annotation { "Feature Type Name" : "Feature", "Feature Type Description" : "" }
export const myFeature = defineFeature(function(context is Context, id is Id, definition is map)
    precondition{}
    {
        {
            var Q0;
            Q0=qCreatedBy(makeId("Top.planeOp"),FACE);
            var sketch = newSketch(context, id + "F0", { "sketchPlane" : qUnion([Q0])});
            skLineSegment(sketch, "E0.bottom", {"start": v(76.5, 51) * mm, "end": v(57.38, 51) * mm});
            skLineSegment(sketch, "E0.top", {"start": v(76.5, -51) * mm, "end": v(-76.5, -51) * mm});
            skLineSegment(sketch, "E0.left", {"start": v(76.5, 51) * mm, "end": v(76.5, -51) * mm});
            skLineSegment(sketch, "E0.right", {"start": v(-76.5, 51) * mm, "end": v(-76.5, 38.25) * mm});
            skPoint(sketch, "E0.middle", {"position": v(0, 0) * mm});
            skLineSegment(sketch, "E1", {"start": v(0, 51) * mm, "end": v(-19.12, 51) * mm});
            skLineSegment(sketch, "E2", {"start": v(-38.25, 51) * mm, "end": v(-57.38, 51) * mm});
            skLineSegment(sketch, "E3", {"start": v(38.25, 51) * mm, "end": v(19.13, 51) * mm});
            skLineSegment(sketch, "E4", {"start": v(-57.38, 51) * mm, "end": v(-76.5, 51) * mm});
            skLineSegment(sketch, "E5", {"start": v(-19.12, 51) * mm, "end": v(-38.25, 51) * mm});
            skLineSegment(sketch, "E6", {"start": v(19.13, 51) * mm, "end": v(0, 51) * mm});
            skLineSegment(sketch, "E7", {"start": v(57.38, 51) * mm, "end": v(38.25, 51) * mm});
            skLineSegment(sketch, "E8", {"start": v(-76.5, 0) * mm, "end": v(-76.5, -12.75) * mm});
            skLineSegment(sketch, "E9", {"start": v(-76.5, 25.5) * mm, "end": v(-76.5, 12.75) * mm});
            skLineSegment(sketch, "E10", {"start": v(-76.5, 38.25) * mm, "end": v(-76.5, 25.5) * mm});
            skLineSegment(sketch, "E11", {"start": v(-76.5, 12.75) * mm, "end": v(-76.5, 0) * mm});
            skLineSegment(sketch, "E12", {"start": v(-76.5, -25.5) * mm, "end": v(-76.5, -38.25) * mm});
            skLineSegment(sketch, "E13", {"start": v(-76.5, -12.75) * mm, "end": v(-76.5, -25.5) * mm});
            skLineSegment(sketch, "E14", {"start": v(-76.5, -38.25) * mm, "end": v(-76.5, -51) * mm});
            skLineSegment(sketch, "E15", {"start": v(-57.38, 51) * mm, "end": v(-57.38, -51) * mm, "construction": true});
            skLineSegment(sketch, "E16", {"start": v(-57.38, -51) * mm, "end": v(-38.25, -51) * mm, "construction": true});
            skLineSegment(sketch, "E17", {"start": v(-38.25, -51) * mm, "end": v(-38.25, 51) * mm, "construction": true});
            skLineSegment(sketch, "E18", {"start": v(-19.12, 51) * mm, "end": v(-19.12, -51) * mm, "construction": true});
            skLineSegment(sketch, "E19", {"start": v(-19.12, -51) * mm, "end": v(0, -51) * mm, "construction": true});
            skLineSegment(sketch, "E20", {"start": v(0, -51) * mm, "end": v(0, 51) * mm, "construction": true});
            skLineSegment(sketch, "E21", {"start": v(19.13, 51) * mm, "end": v(19.13, -51) * mm, "construction": true});
            skLineSegment(sketch, "E22", {"start": v(19.13, -51) * mm, "end": v(38.25, -51) * mm, "construction": true});
            skLineSegment(sketch, "E23", {"start": v(38.25, -51) * mm, "end": v(38.25, 51) * mm, "construction": true});
            skLineSegment(sketch, "E24", {"start": v(57.38, 51) * mm, "end": v(57.38, -51) * mm, "construction": true});
            skLineSegment(sketch, "E25", {"start": v(57.37, -51) * mm, "end": v(-76.5, -51) * mm, "construction": true});
            skLineSegment(sketch, "E26", {"start": v(-76.5, -38.25) * mm, "end": v(76.5, -38.25) * mm, "construction": true});
            skLineSegment(sketch, "E27", {"start": v(76.5, -38.25) * mm, "end": v(76.5, -25.5) * mm, "construction": true});
            skLineSegment(sketch, "E28", {"start": v(76.5, -25.5) * mm, "end": v(-76.5, -25.5) * mm, "construction": true});
            skLineSegment(sketch, "E29", {"start": v(-76.5, -12.75) * mm, "end": v(76.5, -12.75) * mm, "construction": true});
            skLineSegment(sketch, "E30", {"start": v(76.5, -12.75) * mm, "end": v(76.5, 0) * mm, "construction": true});
            skLineSegment(sketch, "E31", {"start": v(76.5, 0) * mm, "end": v(-76.5, 0) * mm, "construction": true});
            skLineSegment(sketch, "E32", {"start": v(-76.5, 12.75) * mm, "end": v(76.5, 12.75) * mm, "construction": true});
            skLineSegment(sketch, "E33", {"start": v(76.5, 12.75) * mm, "end": v(76.5, 25.5) * mm, "construction": true});
            skLineSegment(sketch, "E34", {"start": v(76.5, 25.5) * mm, "end": v(-76.5, 25.5) * mm, "construction": true});
            skLineSegment(sketch, "E35", {"start": v(-76.5, 38.25) * mm, "end": v(76.5, 38.25) * mm, "construction": true});
            skCircle(sketch, "E36", {"center": v(-57.38, 38.25) * mm, "radius": 3.17 * mm});
            skCircle(sketch, "E37", {"center": v(-57.38, 25.5) * mm, "radius": 3.17 * mm});
            skCircle(sketch, "E38", {"center": v(-57.38, 12.75) * mm, "radius": 3.17 * mm});
            skCircle(sketch, "E39", {"center": v(-57.38, 0) * mm, "radius": 3.17 * mm});
            skCircle(sketch, "E40", {"center": v(-57.38, -12.75) * mm, "radius": 3.17 * mm});
            skCircle(sketch, "E41", {"center": v(-57.38, -25.5) * mm, "radius": 3.17 * mm});
            skCircle(sketch, "E42", {"center": v(-57.38, -38.25) * mm, "radius": 3.17 * mm});
            skCircle(sketch, "E43.1.0.0", {"center": v(-38.25, 38.25) * mm, "radius": 3.17 * mm});
            skCircle(sketch, "E43.1.0.1", {"center": v(-38.25, 25.5) * mm, "radius": 3.17 * mm});
            skCircle(sketch, "E43.1.0.2", {"center": v(-38.25, -38.25) * mm, "radius": 3.17 * mm});
            skCircle(sketch, "E43.1.0.3", {"center": v(-38.25, 12.75) * mm, "radius": 3.17 * mm});
            skCircle(sketch, "E43.1.0.4", {"center": v(-38.25, 0) * mm, "radius": 3.17 * mm});
            skCircle(sketch, "E43.1.0.5", {"center": v(-38.25, -12.75) * mm, "radius": 3.17 * mm});
            skCircle(sketch, "E43.1.0.6", {"center": v(-38.25, -25.5) * mm, "radius": 3.17 * mm});
            skCircle(sketch, "E43.2.0.0", {"center": v(-19.13, 38.25) * mm, "radius": 3.17 * mm});
            skCircle(sketch, "E43.2.0.1", {"center": v(-19.13, 25.5) * mm, "radius": 3.17 * mm});
            skCircle(sketch, "E43.2.0.2", {"center": v(-19.13, -38.25) * mm, "radius": 3.17 * mm});
            skCircle(sketch, "E43.2.0.3", {"center": v(-19.13, 12.75) * mm, "radius": 3.17 * mm});
            skCircle(sketch, "E43.2.0.4", {"center": v(-19.13, 0) * mm, "radius": 3.17 * mm});
            skCircle(sketch, "E43.2.0.5", {"center": v(-19.13, -12.75) * mm, "radius": 3.17 * mm});
            skCircle(sketch, "E43.2.0.6", {"center": v(-19.13, -25.5) * mm, "radius": 3.17 * mm});
            skCircle(sketch, "E43.3.0.0", {"center": v(0, 38.25) * mm, "radius": 3.17 * mm});
            skCircle(sketch, "E43.3.0.1", {"center": v(0, 25.5) * mm, "radius": 3.17 * mm});
            skCircle(sketch, "E43.3.0.2", {"center": v(0, -38.25) * mm, "radius": 3.17 * mm});
            skCircle(sketch, "E43.3.0.3", {"center": v(0, 12.75) * mm, "radius": 3.17 * mm});
            skCircle(sketch, "E43.3.0.4", {"center": v(0, 0) * mm, "radius": 3.17 * mm});
            skCircle(sketch, "E43.3.0.5", {"center": v(0, -12.75) * mm, "radius": 3.17 * mm});
            skCircle(sketch, "E43.3.0.6", {"center": v(0, -25.5) * mm, "radius": 3.17 * mm});
            skCircle(sketch, "E43.4.0.0", {"center": v(19.12, 38.25) * mm, "radius": 3.17 * mm});
            skCircle(sketch, "E43.4.0.1", {"center": v(19.12, 25.5) * mm, "radius": 3.17 * mm});
            skCircle(sketch, "E43.4.0.2", {"center": v(19.12, -38.25) * mm, "radius": 3.17 * mm});
            skCircle(sketch, "E43.4.0.3", {"center": v(19.12, 12.75) * mm, "radius": 3.17 * mm});
            skCircle(sketch, "E43.4.0.4", {"center": v(19.12, 0) * mm, "radius": 3.17 * mm});
            skCircle(sketch, "E43.4.0.5", {"center": v(19.12, -12.75) * mm, "radius": 3.17 * mm});
            skCircle(sketch, "E43.4.0.6", {"center": v(19.12, -25.5) * mm, "radius": 3.17 * mm});
            skCircle(sketch, "E43.5.0.0", {"center": v(38.25, 38.25) * mm, "radius": 3.17 * mm});
            skCircle(sketch, "E43.5.0.1", {"center": v(38.25, 25.5) * mm, "radius": 3.17 * mm});
            skCircle(sketch, "E43.5.0.2", {"center": v(38.25, -38.25) * mm, "radius": 3.17 * mm});
            skCircle(sketch, "E43.5.0.3", {"center": v(38.25, 12.75) * mm, "radius": 3.17 * mm});
            skCircle(sketch, "E43.5.0.4", {"center": v(38.25, 0) * mm, "radius": 3.17 * mm});
            skCircle(sketch, "E43.5.0.5", {"center": v(38.25, -12.75) * mm, "radius": 3.17 * mm});
            skCircle(sketch, "E43.5.0.6", {"center": v(38.25, -25.5) * mm, "radius": 3.17 * mm});
            skCircle(sketch, "E43.6.0.0", {"center": v(57.37, 38.25) * mm, "radius": 3.17 * mm});
            skCircle(sketch, "E43.6.0.1", {"center": v(57.37, 25.5) * mm, "radius": 3.17 * mm});
            skCircle(sketch, "E43.6.0.2", {"center": v(57.37, -38.25) * mm, "radius": 3.17 * mm});
            skCircle(sketch, "E43.6.0.3", {"center": v(57.37, 12.75) * mm, "radius": 3.17 * mm});
            skCircle(sketch, "E43.6.0.4", {"center": v(57.37, 0) * mm, "radius": 3.17 * mm});
            skCircle(sketch, "E43.6.0.5", {"center": v(57.37, -12.75) * mm, "radius": 3.17 * mm});
            skCircle(sketch, "E43.6.0.6", {"center": v(57.37, -25.5) * mm, "radius": 3.17 * mm});
            skLineSegment(sketch, "E43.direction1", {"start": v(-57.38, -38.25) * mm, "end": v(-38.25, -38.25) * mm, "construction": true});
            skSolve(sketch);
        }
        {
            var Q0;
            Q0=makeQuery(id+"F0.imprint","IMPRINT",FACE,{"disambiguationData":[TD([[makeQuery(id+"F0.imprint","IMPRINT",EDGE,{"derivedFrom":sQuery(id+"F0.wireOp",EDGE,"E0.bottom")}),1.0]])]});
            extrude(context, id + "F1", {"entities" : qUnion([Q0]), "depth" : 25 * mm, "offsetDistance" : 25 * mm});
        }
        {
            var Q0;
            Q0=makeQuery(id+"F1.opExtrude","CAP_FACE",FACE,{"disambiguationData":[OSD([sQuery(id+"F0.wireOp",EDGE,"E0.bottom"),sQuery(id+"F0.wireOp",EDGE,"E0.top"),sQuery(id+"F0.wireOp",EDGE,"E0.left"),sQuery(id+"F0.wireOp",EDGE,"E0.right"),sQuery(id+"F0.wireOp",EDGE,"E1"),sQuery(id+"F0.wireOp",EDGE,"E2"),sQuery(id+"F0.wireOp",EDGE,"E3"),sQuery(id+"F0.wireOp",EDGE,"E4"),sQuery(id+"F0.wireOp",EDGE,"E5"),sQuery(id+"F0.wireOp",EDGE,"E6"),sQuery(id+"F0.wireOp",EDGE,"E7"),sQuery(id+"F0.wireOp",EDGE,"E8"),sQuery(id+"F0.wireOp",EDGE,"E9"),sQuery(id+"F0.wireOp",EDGE,"E10"),sQuery(id+"F0.wireOp",EDGE,"E11"),sQuery(id+"F0.wireOp",EDGE,"E12"),sQuery(id+"F0.wireOp",EDGE,"E13"),sQuery(id+"F0.wireOp",EDGE,"E14"),sQuery(id+"F0.wireOp",EDGE,"E36"),sQuery(id+"F0.wireOp",EDGE,"E37"),sQuery(id+"F0.wireOp",EDGE,"E38"),sQuery(id+"F0.wireOp",EDGE,"E39"),sQuery(id+"F0.wireOp",EDGE,"E40"),sQuery(id+"F0.wireOp",EDGE,"E41"),sQuery(id+"F0.wireOp",EDGE,"E42"),sQuery(id+"F0.wireOp",EDGE,"E43.1.0.0"),sQuery(id+"F0.wireOp",EDGE,"E43.1.0.1"),sQuery(id+"F0.wireOp",EDGE,"E43.1.0.2"),sQuery(id+"F0.wireOp",EDGE,"E43.1.0.3"),sQuery(id+"F0.wireOp",EDGE,"E43.1.0.4"),sQuery(id+"F0.wireOp",EDGE,"E43.1.0.5"),sQuery(id+"F0.wireOp",EDGE,"E43.1.0.6"),sQuery(id+"F0.wireOp",EDGE,"E43.2.0.0"),sQuery(id+"F0.wireOp",EDGE,"E43.2.0.1"),sQuery(id+"F0.wireOp",EDGE,"E43.2.0.2"),sQuery(id+"F0.wireOp",EDGE,"E43.2.0.3"),sQuery(id+"F0.wireOp",EDGE,"E43.2.0.4"),sQuery(id+"F0.wireOp",EDGE,"E43.2.0.5"),sQuery(id+"F0.wireOp",EDGE,"E43.2.0.6"),sQuery(id+"F0.wireOp",EDGE,"E43.3.0.0"),sQuery(id+"F0.wireOp",EDGE,"E43.3.0.1"),sQuery(id+"F0.wireOp",EDGE,"E43.3.0.2"),sQuery(id+"F0.wireOp",EDGE,"E43.3.0.3"),sQuery(id+"F0.wireOp",EDGE,"E43.3.0.4"),sQuery(id+"F0.wireOp",EDGE,"E43.3.0.5"),sQuery(id+"F0.wireOp",EDGE,"E43.3.0.6"),sQuery(id+"F0.wireOp",EDGE,"E43.4.0.0"),sQuery(id+"F0.wireOp",EDGE,"E43.4.0.1"),sQuery(id+"F0.wireOp",EDGE,"E43.4.0.2"),sQuery(id+"F0.wireOp",EDGE,"E43.4.0.3"),sQuery(id+"F0.wireOp",EDGE,"E43.4.0.4"),sQuery(id+"F0.wireOp",EDGE,"E43.4.0.5"),sQuery(id+"F0.wireOp",EDGE,"E43.4.0.6"),sQuery(id+"F0.wireOp",EDGE,"E43.5.0.0"),sQuery(id+"F0.wireOp",EDGE,"E43.5.0.1"),sQuery(id+"F0.wireOp",EDGE,"E43.5.0.2"),sQuery(id+"F0.wireOp",EDGE,"E43.5.0.3"),sQuery(id+"F0.wireOp",EDGE,"E43.5.0.4"),sQuery(id+"F0.wireOp",EDGE,"E43.5.0.5"),sQuery(id+"F0.wireOp",EDGE,"E43.5.0.6"),sQuery(id+"F0.wireOp",EDGE,"E43.6.0.0"),sQuery(id+"F0.wireOp",EDGE,"E43.6.0.1"),sQuery(id+"F0.wireOp",EDGE,"E43.6.0.2"),sQuery(id+"F0.wireOp",EDGE,"E43.6.0.3"),sQuery(id+"F0.wireOp",EDGE,"E43.6.0.4"),sQuery(id+"F0.wireOp",EDGE,"E43.6.0.5"),sQuery(id+"F0.wireOp",EDGE,"E43.6.0.6")])],"isStart":false});
            var sketch = newSketch(context, id + "F2", { "sketchPlane" : qUnion([Q0])});
            skLineSegment(sketch, "E44.0", {"start": v(74.1, 48.6) * mm, "end": v(-74.1, 48.6) * mm});
            skLineSegment(sketch, "E44.1", {"start": v(74.1, 48.6) * mm, "end": v(74.1, -48.6) * mm});
            skLineSegment(sketch, "E44.2", {"start": v(74.1, -48.6) * mm, "end": v(-74.1, -48.6) * mm});
            skLineSegment(sketch, "E44.3", {"start": v(-74.1, 48.6) * mm, "end": v(-74.1, -48.6) * mm});
            skSolve(sketch);
        }
        {
            var Q0;
            Q0=makeQuery(id+"F2.imprint","IMPRINT",FACE,{"disambiguationData":[TD([[makeQuery(id+"F2.imprint","IMPRINT",EDGE,{"derivedFrom":sQuery(id+"F2.wireOp",EDGE,"E44.0")}),-1.0]])]});
            extrude(context, id + "F3", {"entities" : qUnion([Q0]), "operationType" : NewBodyOperationType.ADD, "depth" : 32.5 * mm, "offsetDistance" : 25 * mm});
        }
        {
            var Q0;
            Q0=makeQuery(id+"F1.opExtrude","CAP_FACE",FACE,{"disambiguationData":[OSD([sQuery(id+"F0.wireOp",EDGE,"E0.bottom"),sQuery(id+"F0.wireOp",EDGE,"E0.top"),sQuery(id+"F0.wireOp",EDGE,"E0.left"),sQuery(id+"F0.wireOp",EDGE,"E0.right"),sQuery(id+"F0.wireOp",EDGE,"E1"),sQuery(id+"F0.wireOp",EDGE,"E2"),sQuery(id+"F0.wireOp",EDGE,"E3"),sQuery(id+"F0.wireOp",EDGE,"E4"),sQuery(id+"F0.wireOp",EDGE,"E5"),sQuery(id+"F0.wireOp",EDGE,"E6"),sQuery(id+"F0.wireOp",EDGE,"E7"),sQuery(id+"F0.wireOp",EDGE,"E8"),sQuery(id+"F0.wireOp",EDGE,"E9"),sQuery(id+"F0.wireOp",EDGE,"E10"),sQuery(id+"F0.wireOp",EDGE,"E11"),sQuery(id+"F0.wireOp",EDGE,"E12"),sQuery(id+"F0.wireOp",EDGE,"E13"),sQuery(id+"F0.wireOp",EDGE,"E14"),sQuery(id+"F0.wireOp",EDGE,"E36"),sQuery(id+"F0.wireOp",EDGE,"E37"),sQuery(id+"F0.wireOp",EDGE,"E38"),sQuery(id+"F0.wireOp",EDGE,"E39"),sQuery(id+"F0.wireOp",EDGE,"E40"),sQuery(id+"F0.wireOp",EDGE,"E41"),sQuery(id+"F0.wireOp",EDGE,"E42"),sQuery(id+"F0.wireOp",EDGE,"E43.1.0.0"),sQuery(id+"F0.wireOp",EDGE,"E43.1.0.1"),sQuery(id+"F0.wireOp",EDGE,"E43.1.0.2"),sQuery(id+"F0.wireOp",EDGE,"E43.1.0.3"),sQuery(id+"F0.wireOp",EDGE,"E43.1.0.4"),sQuery(id+"F0.wireOp",EDGE,"E43.1.0.5"),sQuery(id+"F0.wireOp",EDGE,"E43.1.0.6"),sQuery(id+"F0.wireOp",EDGE,"E43.2.0.0"),sQuery(id+"F0.wireOp",EDGE,"E43.2.0.1"),sQuery(id+"F0.wireOp",EDGE,"E43.2.0.2"),sQuery(id+"F0.wireOp",EDGE,"E43.2.0.3"),sQuery(id+"F0.wireOp",EDGE,"E43.2.0.4"),sQuery(id+"F0.wireOp",EDGE,"E43.2.0.5"),sQuery(id+"F0.wireOp",EDGE,"E43.2.0.6"),sQuery(id+"F0.wireOp",EDGE,"E43.3.0.0"),sQuery(id+"F0.wireOp",EDGE,"E43.3.0.1"),sQuery(id+"F0.wireOp",EDGE,"E43.3.0.2"),sQuery(id+"F0.wireOp",EDGE,"E43.3.0.3"),sQuery(id+"F0.wireOp",EDGE,"E43.3.0.4"),sQuery(id+"F0.wireOp",EDGE,"E43.3.0.5"),sQuery(id+"F0.wireOp",EDGE,"E43.3.0.6"),sQuery(id+"F0.wireOp",EDGE,"E43.4.0.0"),sQuery(id+"F0.wireOp",EDGE,"E43.4.0.1"),sQuery(id+"F0.wireOp",EDGE,"E43.4.0.2"),sQuery(id+"F0.wireOp",EDGE,"E43.4.0.3"),sQuery(id+"F0.wireOp",EDGE,"E43.4.0.4"),sQuery(id+"F0.wireOp",EDGE,"E43.4.0.5"),sQuery(id+"F0.wireOp",EDGE,"E43.4.0.6"),sQuery(id+"F0.wireOp",EDGE,"E43.5.0.0"),sQuery(id+"F0.wireOp",EDGE,"E43.5.0.1"),sQuery(id+"F0.wireOp",EDGE,"E43.5.0.2"),sQuery(id+"F0.wireOp",EDGE,"E43.5.0.3"),sQuery(id+"F0.wireOp",EDGE,"E43.5.0.4"),sQuery(id+"F0.wireOp",EDGE,"E43.5.0.5"),sQuery(id+"F0.wireOp",EDGE,"E43.5.0.6"),sQuery(id+"F0.wireOp",EDGE,"E43.6.0.0"),sQuery(id+"F0.wireOp",EDGE,"E43.6.0.1"),sQuery(id+"F0.wireOp",EDGE,"E43.6.0.2"),sQuery(id+"F0.wireOp",EDGE,"E43.6.0.3"),sQuery(id+"F0.wireOp",EDGE,"E43.6.0.4"),sQuery(id+"F0.wireOp",EDGE,"E43.6.0.5"),sQuery(id+"F0.wireOp",EDGE,"E43.6.0.6")])],"isStart":true});
            var sketch = newSketch(context, id + "F4", { "sketchPlane" : qUnion([Q0])});
            skLineSegment(sketch, "E45.bottom", {"start": v(-76.5, 51) * mm, "end": v(76.5, 51) * mm});
            skLineSegment(sketch, "E45.top", {"start": v(-76.5, -51) * mm, "end": v(76.5, -51) * mm});
            skLineSegment(sketch, "E45.left", {"start": v(-76.5, 51) * mm, "end": v(-76.5, -51) * mm});
            skLineSegment(sketch, "E45.right", {"start": v(76.5, 51) * mm, "end": v(76.5, -51) * mm});
            skSolve(sketch);
        }
        {
            var Q0;
            Q0 = qSketchRegion(id + "F4", true);
            extrude(context, id + "F5", {"entities" : qUnion([Q0]), "operationType" : NewBodyOperationType.ADD, "depth" : 2.4 * mm, "offsetDistance" : 25 * mm});
        }
        {
            var Q0;
            Q0=makeQuery(id+"F5.opExtrude","CAP_FACE",FACE,{"disambiguationData":[OSD([sQuery(id+"F4.wireOp",EDGE,"E45.bottom"),sQuery(id+"F4.wireOp",EDGE,"E45.top"),sQuery(id+"F4.wireOp",EDGE,"E45.left"),sQuery(id+"F4.wireOp",EDGE,"E45.right")])],"isStart":false});
            var Q1;
            {var subQ0=sQuery(id+"F0.wireOp",EDGE,"E14");var subQ1=sQuery(id+"F0.wireOp",EDGE,"E0.top");Q1=makeQuery(id+"F5.boolean.opBoolean","MERGE",EDGE,{"derivedFrom":[makeQuery(id+"F3.boolean.opBoolean","MERGE",EDGE,{"derivedFrom":[makeQuery(id+"F1.opExtrude","SWEPT_EDGE",EDGE,{"disambiguationData":[OSD([subQ1,subQ0])]}),makeQuery(id+"F3.opExtrude","SWEPT_EDGE",EDGE,{"disambiguationData":[OSD([subQ1,sQuery(id+"F0.wireOp",EDGE,"E0.right"),sQuery(id+"F0.wireOp",EDGE,"E8"),sQuery(id+"F0.wireOp",EDGE,"E9"),sQuery(id+"F0.wireOp",EDGE,"E10"),sQuery(id+"F0.wireOp",EDGE,"E11"),sQuery(id+"F0.wireOp",EDGE,"E12"),sQuery(id+"F0.wireOp",EDGE,"E13"),subQ0])]})]}),makeQuery(id+"F5.opExtrude","SWEPT_EDGE",EDGE,{"disambiguationData":[OSD([sQuery(id+"F4.wireOp",EDGE,"E45.bottom"),sQuery(id+"F4.wireOp",EDGE,"E45.left")])]})]});}
            var Q2;
            {var subQ0=sQuery(id+"F0.wireOp",EDGE,"E4");var subQ1=sQuery(id+"F0.wireOp",EDGE,"E0.right");Q2=makeQuery(id+"F5.boolean.opBoolean","MERGE",EDGE,{"derivedFrom":[makeQuery(id+"F3.boolean.opBoolean","MERGE",EDGE,{"derivedFrom":[makeQuery(id+"F1.opExtrude","SWEPT_EDGE",EDGE,{"disambiguationData":[OSD([subQ1,subQ0])]}),makeQuery(id+"F3.opExtrude","SWEPT_EDGE",EDGE,{"disambiguationData":[OSD([sQuery(id+"F0.wireOp",EDGE,"E0.bottom"),subQ1,sQuery(id+"F0.wireOp",EDGE,"E1"),sQuery(id+"F0.wireOp",EDGE,"E2"),sQuery(id+"F0.wireOp",EDGE,"E3"),subQ0,sQuery(id+"F0.wireOp",EDGE,"E5"),sQuery(id+"F0.wireOp",EDGE,"E6"),sQuery(id+"F0.wireOp",EDGE,"E7"),sQuery(id+"F0.wireOp",EDGE,"E8"),sQuery(id+"F0.wireOp",EDGE,"E9"),sQuery(id+"F0.wireOp",EDGE,"E10"),sQuery(id+"F0.wireOp",EDGE,"E11"),sQuery(id+"F0.wireOp",EDGE,"E12"),sQuery(id+"F0.wireOp",EDGE,"E13"),sQuery(id+"F0.wireOp",EDGE,"E14")])]})]}),makeQuery(id+"F5.opExtrude","SWEPT_EDGE",EDGE,{"disambiguationData":[OSD([sQuery(id+"F4.wireOp",EDGE,"E45.top"),sQuery(id+"F4.wireOp",EDGE,"E45.left")])]})]});}
            var Q3;
            {var subQ0=sQuery(id+"F0.wireOp",EDGE,"E0.left");var subQ1=sQuery(id+"F0.wireOp",EDGE,"E0.bottom");Q3=makeQuery(id+"F5.boolean.opBoolean","MERGE",EDGE,{"derivedFrom":[makeQuery(id+"F3.boolean.opBoolean","MERGE",EDGE,{"derivedFrom":[makeQuery(id+"F1.opExtrude","SWEPT_EDGE",EDGE,{"disambiguationData":[OSD([subQ1,subQ0])]}),makeQuery(id+"F3.opExtrude","SWEPT_EDGE",EDGE,{"disambiguationData":[OSD([subQ1,subQ0,sQuery(id+"F0.wireOp",EDGE,"E1"),sQuery(id+"F0.wireOp",EDGE,"E2"),sQuery(id+"F0.wireOp",EDGE,"E3"),sQuery(id+"F0.wireOp",EDGE,"E4"),sQuery(id+"F0.wireOp",EDGE,"E5"),sQuery(id+"F0.wireOp",EDGE,"E6"),sQuery(id+"F0.wireOp",EDGE,"E7")])]})]}),makeQuery(id+"F5.opExtrude","SWEPT_EDGE",EDGE,{"disambiguationData":[OSD([sQuery(id+"F4.wireOp",EDGE,"E45.top"),sQuery(id+"F4.wireOp",EDGE,"E45.right")])]})]});}
            var Q4;
            {var subQ0=sQuery(id+"F0.wireOp",EDGE,"E0.left");var subQ1=sQuery(id+"F0.wireOp",EDGE,"E0.top");Q4=makeQuery(id+"F5.boolean.opBoolean","MERGE",EDGE,{"derivedFrom":[makeQuery(id+"F3.boolean.opBoolean","MERGE",EDGE,{"derivedFrom":[makeQuery(id+"F1.opExtrude","SWEPT_EDGE",EDGE,{"disambiguationData":[OSD([subQ1,subQ0])]}),makeQuery(id+"F3.opExtrude","SWEPT_EDGE",EDGE,{"disambiguationData":[OSD([subQ1,subQ0])]})]}),makeQuery(id+"F5.opExtrude","SWEPT_EDGE",EDGE,{"disambiguationData":[OSD([sQuery(id+"F4.wireOp",EDGE,"E45.bottom"),sQuery(id+"F4.wireOp",EDGE,"E45.right")])]})]});}
            fillet(context, id + "F6", {"entities" : qUnion([Q0, Q1, Q2, Q3, Q4]), "radius" : 2.5 * mm, "tangentPropagation" : true, "allowEdgeOverflow" : false});
        }
        {
            var Q0;
            Q0=makeQuery(id+"F3.opExtrude","CAP_FACE",FACE,{"disambiguationData":[OSD([sQuery(id+"F0.wireOp",EDGE,"E0.bottom"),sQuery(id+"F0.wireOp",EDGE,"E0.top"),sQuery(id+"F0.wireOp",EDGE,"E0.left"),sQuery(id+"F0.wireOp",EDGE,"E0.right"),sQuery(id+"F0.wireOp",EDGE,"E1"),sQuery(id+"F0.wireOp",EDGE,"E2"),sQuery(id+"F0.wireOp",EDGE,"E3"),sQuery(id+"F0.wireOp",EDGE,"E4"),sQuery(id+"F0.wireOp",EDGE,"E5"),sQuery(id+"F0.wireOp",EDGE,"E6"),sQuery(id+"F0.wireOp",EDGE,"E7"),sQuery(id+"F0.wireOp",EDGE,"E8"),sQuery(id+"F0.wireOp",EDGE,"E9"),sQuery(id+"F0.wireOp",EDGE,"E10"),sQuery(id+"F0.wireOp",EDGE,"E11"),sQuery(id+"F0.wireOp",EDGE,"E12"),sQuery(id+"F0.wireOp",EDGE,"E13"),sQuery(id+"F0.wireOp",EDGE,"E14"),sQuery(id+"F2.wireOp",EDGE,"E44.0"),sQuery(id+"F2.wireOp",EDGE,"E44.1"),sQuery(id+"F2.wireOp",EDGE,"E44.2"),sQuery(id+"F2.wireOp",EDGE,"E44.3")])],"isStart":false});
            var sketch = newSketch(context, id + "F7", { "sketchPlane" : qUnion([Q0])});
            skLineSegment(sketch, "E46.bottom", {"start": v(-76.5, 51) * mm, "end": v(76.5, 51) * mm});
            skLineSegment(sketch, "E46.top", {"start": v(-76.5, -51) * mm, "end": v(76.5, -51) * mm});
            skLineSegment(sketch, "E46.left", {"start": v(-76.5, 51) * mm, "end": v(-76.5, -51) * mm});
            skLineSegment(sketch, "E46.right", {"start": v(76.5, 51) * mm, "end": v(76.5, -51) * mm});
            skSolve(sketch);
        }
        {
            var Q0;
            Q0 = qSketchRegion(id + "F7", true);
            var Q1;
            Q1=makeQuery(id+"F5.opExtrude","CAP_FACE",FACE,{"disambiguationData":[OSD([sQuery(id+"F4.wireOp",EDGE,"E45.bottom"),sQuery(id+"F4.wireOp",EDGE,"E45.top"),sQuery(id+"F4.wireOp",EDGE,"E45.left"),sQuery(id+"F4.wireOp",EDGE,"E45.right")])],"isStart":false});
            extrude(context, id + "F8", {"entities" : qUnion([Q0]), "endBound" : BoundingType.UP_TO_SURFACE, "oppositeDirection" : true, "depth" : 25 * mm, "endBoundEntityFace" : qUnion([Q1]), "offsetDistance" : 25 * mm});
        }
        {
            var Q0;
            Q0=makeQuery(id+"F8.opExtrude","CAP_FACE",FACE,{"disambiguationData":[OSD([sQuery(id+"F7.wireOp",EDGE,"E46.bottom"),sQuery(id+"F7.wireOp",EDGE,"E46.top"),sQuery(id+"F7.wireOp",EDGE,"E46.left"),sQuery(id+"F7.wireOp",EDGE,"E46.right")])],"isStart":false});
            shell(context, id + "F9", {"entities" : qUnion([Q0]), "thickness" : 2.9 * mm, "oppositeDirection" : true});
        }
        {
            var Q0;
            Q0=makeQuery(id+"F8.opExtrude","CAP_FACE",FACE,{"disambiguationData":[OSD([sQuery(id+"F7.wireOp",EDGE,"E46.bottom"),sQuery(id+"F7.wireOp",EDGE,"E46.top"),sQuery(id+"F7.wireOp",EDGE,"E46.left"),sQuery(id+"F7.wireOp",EDGE,"E46.right")])],"isStart":true});
            fillet(context, id + "F10", {"entities" : qUnion([Q0]), "radius" : 5 * mm, "tangentPropagation" : true, "allowEdgeOverflow" : false});
        }
        {
            var Q0;
            Q0=makeQuery(id+"F8.opExtrude","CAP_FACE",FACE,{"disambiguationData":[OSD([sQuery(id+"F7.wireOp",EDGE,"E46.bottom"),sQuery(id+"F7.wireOp",EDGE,"E46.top"),sQuery(id+"F7.wireOp",EDGE,"E46.left"),sQuery(id+"F7.wireOp",EDGE,"E46.right")])],"isStart":true});
            var sketch = newSketch(context, id + "F11", { "sketchPlane" : qUnion([Q0])});
            skText(sketch, "E47", { "text": "ROUTER BITS", "fontName": "OpenSans-Bold.ttf"});
            const initialGuessF11  = {"E47": [-0.0709, -0.00018, 1, 0, 0.01591]};
            skSetInitialGuess(sketch, initialGuessF11);
            skSolve(sketch);
        }
        {
            var Q0;
            Q0=makeQuery(id+"F11.imprint","IMPRINT",FACE,{"disambiguationData":[TD([[makeQuery(id+"F11.imprint","IMPRINT",EDGE,{"derivedFrom":sQuery(id+"F11.wireOp",EDGE,"E47.sketch_text.stroke-0")}),-1.0]])]});
            var Q1;
            Q1=makeQuery(id+"F11.imprint","IMPRINT",FACE,{"disambiguationData":[TD([[makeQuery(id+"F11.imprint","IMPRINT",EDGE,{"derivedFrom":sQuery(id+"F11.wireOp",EDGE,"E47.sketch_text.stroke-19")}),-1.0]])]});
            var Q2;
            Q2=makeQuery(id+"F11.imprint","IMPRINT",FACE,{"disambiguationData":[TD([[makeQuery(id+"F11.imprint","IMPRINT",EDGE,{"derivedFrom":sQuery(id+"F11.wireOp",EDGE,"E47.sketch_text.stroke-33")}),-1.0]])]});
            var Q3;
            Q3=makeQuery(id+"F11.imprint","IMPRINT",FACE,{"disambiguationData":[TD([[makeQuery(id+"F11.imprint","IMPRINT",EDGE,{"derivedFrom":sQuery(id+"F11.wireOp",EDGE,"E47.sketch_text.stroke-48")}),-1.0]])]});
            var Q4;
            Q4=makeQuery(id+"F11.imprint","IMPRINT",FACE,{"disambiguationData":[TD([[makeQuery(id+"F11.imprint","IMPRINT",EDGE,{"derivedFrom":sQuery(id+"F11.wireOp",EDGE,"E47.sketch_text.stroke-56")}),-1.0]])]});
            var Q5;
            Q5=makeQuery(id+"F11.imprint","IMPRINT",FACE,{"disambiguationData":[TD([[makeQuery(id+"F11.imprint","IMPRINT",EDGE,{"derivedFrom":sQuery(id+"F11.wireOp",EDGE,"E47.sketch_text.stroke-68")}),-1.0]])]});
            var Q6;
            Q6=makeQuery(id+"F11.imprint","IMPRINT",FACE,{"disambiguationData":[TD([[makeQuery(id+"F11.imprint","IMPRINT",EDGE,{"derivedFrom":sQuery(id+"F11.wireOp",EDGE,"E47.sketch_text.stroke-87")}),-1.0]])]});
            var Q7;
            Q7=makeQuery(id+"F11.imprint","IMPRINT",FACE,{"disambiguationData":[TD([[makeQuery(id+"F11.imprint","IMPRINT",EDGE,{"derivedFrom":sQuery(id+"F11.wireOp",EDGE,"E47.sketch_text.stroke-112")}),-1.0]])]});
            var Q8;
            Q8=makeQuery(id+"F11.imprint","IMPRINT",FACE,{"disambiguationData":[TD([[makeQuery(id+"F11.imprint","IMPRINT",EDGE,{"derivedFrom":sQuery(id+"F11.wireOp",EDGE,"E47.sketch_text.stroke-116")}),-1.0]])]});
            var Q9;
            Q9=makeQuery(id+"F11.imprint","IMPRINT",FACE,{"disambiguationData":[TD([[makeQuery(id+"F11.imprint","IMPRINT",EDGE,{"derivedFrom":sQuery(id+"F11.wireOp",EDGE,"E47.sketch_text.stroke-124")}),-1.0]])]});
            extrude(context, id + "F12", {"entities" : qUnion([Q0, Q1, Q2, Q3, Q4, Q5, Q6, Q7, Q8, Q9]), "operationType" : NewBodyOperationType.REMOVE, "oppositeDirection" : true, "depth" : 1 * mm, "offsetDistance" : 25 * mm});
        }
        {
            var Q0;
            Q0=makeQuery(id+"F12.boolean.opBoolean","COPY",EDGE,{"derivedFrom":makeQuery(id+"F12.opExtrude","CAP_EDGE",EDGE,{"disambiguationData":[OSD([sQuery(id+"F11.wireOp",EDGE,"E47.sketch_text.stroke-9")])],"isStart":true})});
            var Q1;
            {var subQ0=sQuery(id+"F7.wireOp",EDGE,"E46.right");var subQ1=sQuery(id+"F7.wireOp",EDGE,"E46.left");var subQ2=sQuery(id+"F7.wireOp",EDGE,"E46.top");var subQ3=sQuery(id+"F7.wireOp",EDGE,"E46.bottom");Q1=makeQuery(id+"F12.boolean.opBoolean","SPLIT",FACE,{"disambiguationData":[TD([makeQuery(id+"F10.opFillet","BLEND_FACE",FACE,{"disambiguationData":[OSD([subQ3])]})])],"derivedFrom":makeQuery(id+"F8.opExtrude","CAP_FACE",FACE,{"disambiguationData":[OSD([subQ3,subQ2,subQ1,subQ0])],"isStart":true})});}
            var Q2;
            Q2=makeQuery(id+"F12.boolean.opBoolean","SPLIT",FACE,{"disambiguationData":[TD([makeQuery(id+"F12.opExtrude","SWEPT_FACE",FACE,{"disambiguationData":[OSD([sQuery(id+"F11.wireOp",EDGE,"E47.sketch_text.stroke-27")])]})])],"derivedFrom":makeQuery(id+"F8.opExtrude","CAP_FACE",FACE,{"disambiguationData":[OSD([sQuery(id+"F7.wireOp",EDGE,"E46.bottom"),sQuery(id+"F7.wireOp",EDGE,"E46.top"),sQuery(id+"F7.wireOp",EDGE,"E46.left"),sQuery(id+"F7.wireOp",EDGE,"E46.right")])],"isStart":true})});
            var Q3;
            Q3=makeQuery(id+"F12.boolean.opBoolean","SPLIT",FACE,{"disambiguationData":[TD([makeQuery(id+"F12.opExtrude","SWEPT_FACE",FACE,{"disambiguationData":[OSD([sQuery(id+"F11.wireOp",EDGE,"E47.sketch_text.stroke-0")])]})])],"derivedFrom":makeQuery(id+"F8.opExtrude","CAP_FACE",FACE,{"disambiguationData":[OSD([sQuery(id+"F7.wireOp",EDGE,"E46.bottom"),sQuery(id+"F7.wireOp",EDGE,"E46.top"),sQuery(id+"F7.wireOp",EDGE,"E46.left"),sQuery(id+"F7.wireOp",EDGE,"E46.right")])],"isStart":true})});
            var Q4;
            Q4=makeQuery(id+"F12.boolean.opBoolean","SPLIT",FACE,{"disambiguationData":[TD([makeQuery(id+"F12.opExtrude","SWEPT_FACE",FACE,{"disambiguationData":[OSD([sQuery(id+"F11.wireOp",EDGE,"E47.sketch_text.stroke-68")])]})])],"derivedFrom":makeQuery(id+"F8.opExtrude","CAP_FACE",FACE,{"disambiguationData":[OSD([sQuery(id+"F7.wireOp",EDGE,"E46.bottom"),sQuery(id+"F7.wireOp",EDGE,"E46.top"),sQuery(id+"F7.wireOp",EDGE,"E46.left"),sQuery(id+"F7.wireOp",EDGE,"E46.right")])],"isStart":true})});
            var Q5;
            Q5=makeQuery(id+"F12.boolean.opBoolean","SPLIT",FACE,{"disambiguationData":[TD([makeQuery(id+"F12.opExtrude","SWEPT_FACE",FACE,{"disambiguationData":[OSD([sQuery(id+"F11.wireOp",EDGE,"E47.sketch_text.stroke-99")])]})])],"derivedFrom":makeQuery(id+"F8.opExtrude","CAP_FACE",FACE,{"disambiguationData":[OSD([sQuery(id+"F7.wireOp",EDGE,"E46.bottom"),sQuery(id+"F7.wireOp",EDGE,"E46.top"),sQuery(id+"F7.wireOp",EDGE,"E46.left"),sQuery(id+"F7.wireOp",EDGE,"E46.right")])],"isStart":true})});
            var Q6;
            Q6=makeQuery(id+"F12.boolean.opBoolean","SPLIT",FACE,{"disambiguationData":[TD([makeQuery(id+"F12.opExtrude","SWEPT_FACE",FACE,{"disambiguationData":[OSD([sQuery(id+"F11.wireOp",EDGE,"E47.sketch_text.stroke-106")])]})])],"derivedFrom":makeQuery(id+"F8.opExtrude","CAP_FACE",FACE,{"disambiguationData":[OSD([sQuery(id+"F7.wireOp",EDGE,"E46.bottom"),sQuery(id+"F7.wireOp",EDGE,"E46.top"),sQuery(id+"F7.wireOp",EDGE,"E46.left"),sQuery(id+"F7.wireOp",EDGE,"E46.right")])],"isStart":true})});
            fillet(context, id + "F13", {"entities" : qUnion([Q0, Q1, Q2, Q3, Q4, Q5, Q6]), "radius" : 1 * mm, "tangentPropagation" : true, "allowEdgeOverflow" : false});
        }
    });